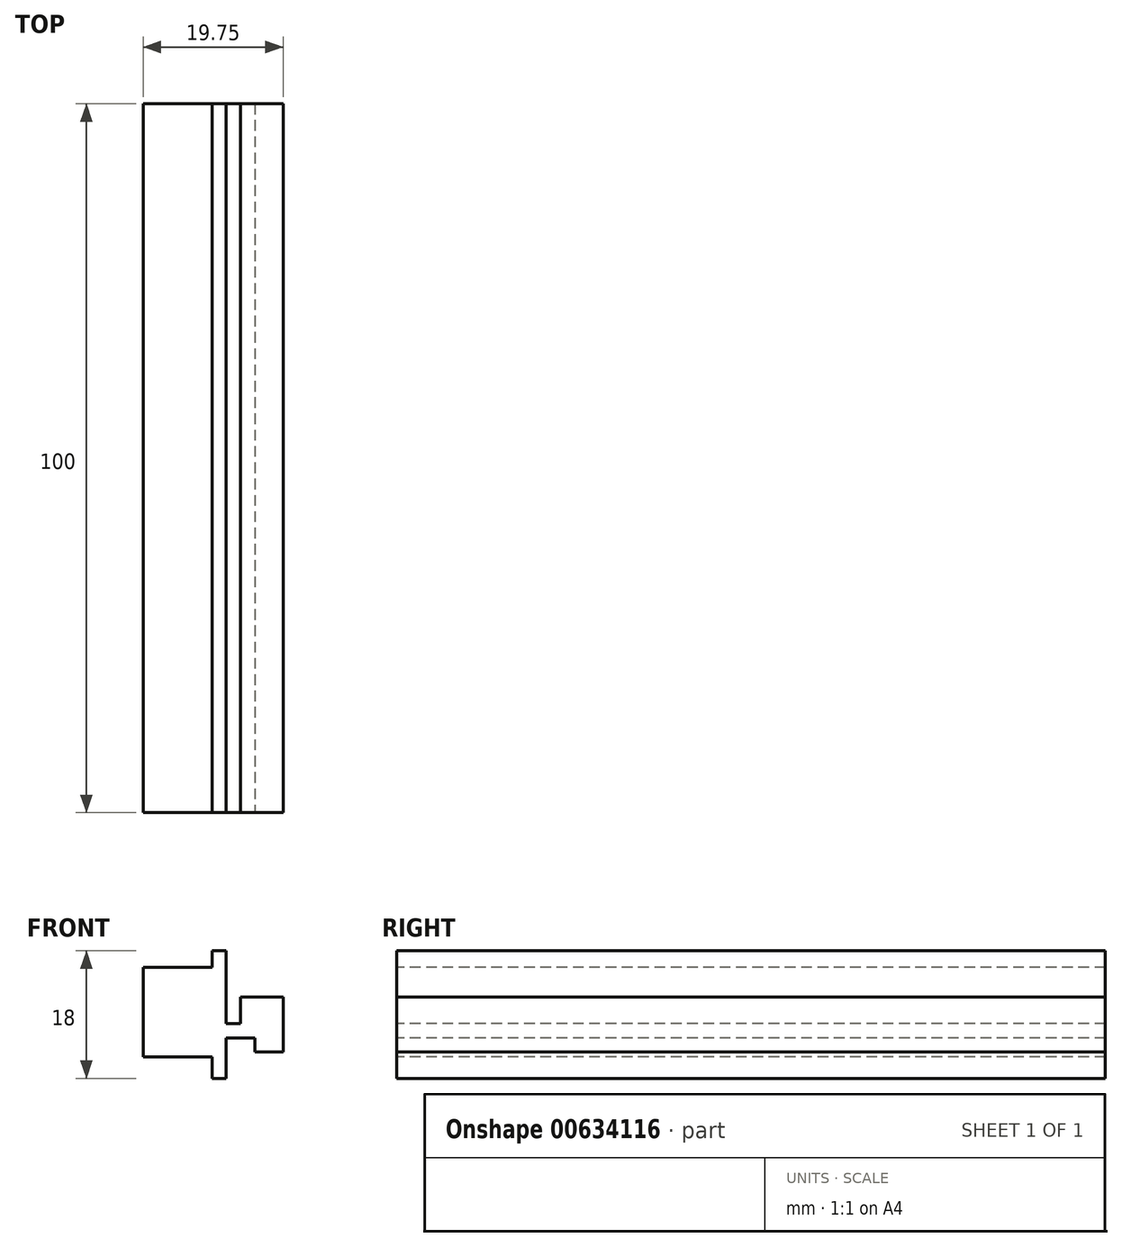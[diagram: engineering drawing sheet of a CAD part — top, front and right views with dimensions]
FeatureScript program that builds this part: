
annotation { "Feature Type Name" : "Feature", "Feature Type Description" : "" }
export const myFeature = defineFeature(function(context is Context, id is Id, definition is map)
    precondition{}
    {
        {
            var Q0;
            Q0=qCreatedBy(makeId("Front.planeOp"),FACE);
            var sketch = newSketch(context, id + "F0", { "sketchPlane" : qUnion([Q0])});
            skLineSegment(sketch, "E0.bottom", {"start": v(-15, 40) * mm, "end": v(15, 40) * mm});
            skLineSegment(sketch, "E0.top", {"start": v(-12, 0) * mm, "end": v(12, 0) * mm});
            skLineSegment(sketch, "E0.left", {"start": v(-15, 40) * mm, "end": v(-15, 37) * mm});
            skLineSegment(sketch, "E0.right", {"start": v(15, 37) * mm, "end": v(15, 3) * mm});
            skLineSegment(sketch, "E1.0", {"start": v(-15, 37) * mm, "end": v(3, 37) * mm});
            skLineSegment(sketch, "E1.1", {"start": v(-12, 6) * mm, "end": v(-12, 6) * mm});
            skLineSegment(sketch, "E1.2", {"start": v(-9, 3) * mm, "end": v(9, 3) * mm});
            skLineSegment(sketch, "E1.3", {"start": v(12, 29.6) * mm, "end": v(12, 6) * mm});
            skLineSegment(sketch, "E2.0", {"start": v(-15, 6) * mm, "end": v(-12, 6) * mm});
            skLineSegment(sketch, "E3", {"start": v(12, 40) * mm, "end": v(7.5, 40) * mm, "construction": true});
            skLineSegment(sketch, "E4", {"start": v(7, 34.8) * mm, "end": v(7, 40) * mm, "construction": true});
            skArc(sketch, "E5", {"start": v(7, 40) * mm, "mid": v(6.75, 29.6) * mm, "end": v(7.5, 39.98) * mm});
            skLineSegment(sketch, "E6.trimOffspring", {"start": v(-15, 6) * mm, "end": v(-15, 3) * mm});
            skPoint(sketch, "E7.orphan", {"position": v(5, 29.7) * mm});
            skPoint(sketch, "E8.visualSharp", {"position": v(15, 40) * mm});
            skArc(sketch, "E8.filletArc", {"start": v(15, 37) * mm, "mid": v(14.12, 39.12) * mm, "end": v(12, 40) * mm});
            skPoint(sketch, "E9.visualSharp", {"position": v(15, 0) * mm});
            skArc(sketch, "E9.filletArc", {"start": v(12, 0) * mm, "mid": v(14.12, 0.88) * mm, "end": v(15, 3) * mm});
            skArc(sketch, "E10.filletArc", {"start": v(9, 3) * mm, "mid": v(11.12, 3.88) * mm, "end": v(12, 6) * mm});
            skPoint(sketch, "E11.visualSharp", {"position": v(-12, 3) * mm});
            skArc(sketch, "E11.filletArc", {"start": v(-12, 6) * mm, "mid": v(-11.12, 3.88) * mm, "end": v(-9, 3) * mm});
            skPoint(sketch, "E12.visualSharp", {"position": v(-15, 0) * mm});
            skArc(sketch, "E12.filletArc", {"start": v(-15, 3) * mm, "mid": v(-14.12, 0.88) * mm, "end": v(-12, 0) * mm});
            skLineSegment(sketch, "E13.0", {"start": v(6.5, 34.8) * mm, "end": v(6.5, 39.8) * mm});
            skLineSegment(sketch, "E14.0", {"start": v(7.5, 34.8) * mm, "end": v(7.5, 40) * mm});
            skLineSegment(sketch, "E15", {"start": v(-15, 6) * mm, "end": v(-15, 16) * mm});
            skLineSegment(sketch, "E16", {"start": v(-15, 16) * mm, "end": v(-12, 16) * mm});
            skLineSegment(sketch, "E17", {"start": v(-12, 16) * mm, "end": v(-12, 6) * mm});
            skLineSegment(sketch, "E18", {"start": v(6.75, 29.6) * mm, "end": v(12, 29.6) * mm});
            skSolve(sketch);
        }
        {
            var Q0;
            Q0=qCreatedBy(makeId("Front.planeOp"),FACE);
            var sketch = newSketch(context, id + "F1", { "sketchPlane" : qUnion([Q0])});
            skLineSegment(sketch, "E19.1.1", {"start": v(7.5, 40) * mm, "end": v(-15, 40) * mm});
            skLineSegment(sketch, "E19.1.2", {"start": v(-15, 40) * mm, "end": v(-15, 37) * mm});
            skArc(sketch, "E19.2.8", {"start": v(-15, 3) * mm, "mid": v(-14.12, 0.88) * mm, "end": v(-12, 0) * mm, "construction": true});
            skLineSegment(sketch, "E19.2.9", {"start": v(-12, 0) * mm, "end": v(-5, 0) * mm});
            skLineSegment(sketch, "E19.2.13", {"start": v(17, 40) * mm, "end": v(8.5, 40) * mm});
            skLineSegment(sketch, "E19.3.0", {"start": v(-15, 18) * mm, "end": v(-15, 7.7) * mm});
            skPoint(sketch, "E20.2", {"position": v(6.5, 37.3) * mm});
            skPoint(sketch, "E21.orphan", {"position": v(6.5, 39.8) * mm});
            skPoint(sketch, "E19.0.2.end.orphan", {"position": v(7, 40) * mm});
            skPoint(sketch, "E22.orphan", {"position": v(12, 29.6) * mm});
            skPoint(sketch, "E23.orphan", {"position": v(7.5, 34.8) * mm});
            skPoint(sketch, "E20.0.start.orphan", {"position": v(6.5, 34.8) * mm});
            skLineSegment(sketch, "E24", {"start": v(-15, 37) * mm, "end": v(-15, 31) * mm});
            skLineSegment(sketch, "E25", {"start": v(0, 0) * mm, "end": v(0, 15) * mm, "construction": true});
            skLineSegment(sketch, "E26", {"start": v(7.5, 40) * mm, "end": v(7.5, 37.97) * mm});
            skLineSegment(sketch, "E27", {"start": v(8.5, 40) * mm, "end": v(8.5, 37.97) * mm});
            skLineSegment(sketch, "E28", {"start": v(15, 32.5) * mm, "end": v(8, 32.5) * mm, "construction": true});
            skPoint(sketch, "E29.orphan", {"position": v(7.6, 39) * mm});
            skLineSegment(sketch, "E30", {"start": v(8, 39) * mm, "end": v(8, 32.5) * mm, "construction": true});
            skPoint(sketch, "E19.3.3.end.orphan", {"position": v(-15, 16) * mm});
            skPoint(sketch, "E19.3.3.start.orphan", {"position": v(-12, 16) * mm});
            skLineSegment(sketch, "E31", {"start": v(-15, 3) * mm, "end": v(-15, 0) * mm});
            skLineSegment(sketch, "E32", {"start": v(-12, 0) * mm, "end": v(-15, 0) * mm});
            skLineSegment(sketch, "E33", {"start": v(-15, 40) * mm, "end": v(-15, 31) * mm, "construction": true});
            skLineSegment(sketch, "E34", {"start": v(-15, 40) * mm, "end": v(-15, 31) * mm});
            skLineSegment(sketch, "E35.trimOffspring", {"start": v(-15, 31) * mm, "end": v(-15, 26) * mm});
            skLineSegment(sketch, "E36.trimOffspring", {"start": v(-15, 29) * mm, "end": v(-15, 24) * mm});
            skPoint(sketch, "E37.orphan", {"position": v(12, 40) * mm});
            skPoint(sketch, "E38.orphan", {"position": v(12, 0) * mm});
            skLineSegment(sketch, "E39.0", {"start": v(13.1, 38) * mm, "end": v(13.1, 38) * mm});
            skLineSegment(sketch, "E40.1", {"start": v(-13, 2) * mm, "end": v(-11, 2) * mm, "construction": true});
            skLineSegment(sketch, "E41.0", {"start": v(-13, 38) * mm, "end": v(-13, 34) * mm});
            skArc(sketch, "E42", {"start": v(13.32, 33.87) * mm, "mid": v(11.56, 36.69) * mm, "end": v(8.5, 37.97) * mm});
            skLineSegment(sketch, "E43.0", {"start": v(29.42, 20) * mm, "end": v(-7, 20) * mm, "construction": true});
            skLineSegment(sketch, "E44.trimOffspring", {"start": v(-13, 0.17) * mm, "end": v(-13, 0) * mm});
            skArc(sketch, "E45.0", {"start": v(2.9, 38) * mm, "mid": v(3.81, 26.3) * mm, "end": v(15, 29.84) * mm});
            skLineSegment(sketch, "E46.trimOffspring", {"start": v(2.9, 38) * mm, "end": v(-13, 38) * mm});
            skLineSegment(sketch, "E47.trimOffspring", {"start": v(13.32, 33.87) * mm, "end": v(13.43, 31.7) * mm});
            skArc(sketch, "E48.trimOffspring", {"start": v(13.1, 38) * mm, "mid": v(13.1, 38) * mm, "end": v(13.1, 38) * mm});
            skArc(sketch, "E49.trimOffspring", {"start": v(7.5, 37.97) * mm, "mid": v(4.01, 28.73) * mm, "end": v(13.43, 31.7) * mm});
            skPoint(sketch, "E50.orphan", {"position": v(7.5, 39) * mm});
            skPoint(sketch, "E51.start.orphan", {"position": v(8.5, 39) * mm});
            skLineSegment(sketch, "E52.0", {"start": v(8, 0) * mm, "end": v(8, 13.5) * mm});
            skLineSegment(sketch, "E53.0", {"start": v(-5, 0) * mm, "end": v(-5, 13.5) * mm});
            skLineSegment(sketch, "E54.0", {"start": v(16.47, 12) * mm, "end": v(14.46, 12) * mm, "construction": true});
            skLineSegment(sketch, "E55.trimOffspring", {"start": v(12.84, 12) * mm, "end": v(10, 12) * mm});
            skLineSegment(sketch, "E56.0", {"start": v(1.5, 0) * mm, "end": v(1.5, 20) * mm, "construction": true});
            skLineSegment(sketch, "E57", {"start": v(1.5, 20) * mm, "end": v(-9.16, 15.5) * mm});
            skLineSegment(sketch, "E58", {"start": v(1.5, 20) * mm, "end": v(10.84, 15.5) * mm});
            skLineSegment(sketch, "E59.0", {"start": v(-9.16, 13.5) * mm, "end": v(-5, 13.5) * mm});
            skLineSegment(sketch, "E60", {"start": v(-9.16, 15.5) * mm, "end": v(-9.16, 13.5) * mm});
            skLineSegment(sketch, "E61", {"start": v(10.84, 15.5) * mm, "end": v(10.84, 13.5) * mm});
            skLineSegment(sketch, "E62.trimOffspring", {"start": v(8, 13.5) * mm, "end": v(10.84, 13.5) * mm});
            skLineSegment(sketch, "E63.trimOffspring", {"start": v(10, 2) * mm, "end": v(15, 2) * mm});
            skLineSegment(sketch, "E64.trimOffspring", {"start": v(8, 0) * mm, "end": v(17, 0) * mm});
            skLineSegment(sketch, "E65.0", {"start": v(10, 2) * mm, "end": v(10, 12) * mm});
            skLineSegment(sketch, "E66.0", {"start": v(1.55, 22.2) * mm, "end": v(-7, 18.58) * mm});
            skLineSegment(sketch, "E66.1", {"start": v(1.55, 22.2) * mm, "end": v(12.84, 16.75) * mm});
            skLineSegment(sketch, "E67.0", {"start": v(-11.16, 16.82) * mm, "end": v(-11.16, 15.5) * mm});
            skLineSegment(sketch, "E68.0", {"start": v(-13, 11.5) * mm, "end": v(-7, 11.5) * mm});
            skLineSegment(sketch, "E69", {"start": v(-11.16, 15.5) * mm, "end": v(-11.16, 13.5) * mm});
            skLineSegment(sketch, "E70.0", {"start": v(12.84, 16.75) * mm, "end": v(12.84, 12) * mm});
            skLineSegment(sketch, "E71.0", {"start": v(-13, 6.7) * mm, "end": v(-7, 6.7) * mm, "construction": true});
            skLineSegment(sketch, "E72.0", {"start": v(-15, 7.7) * mm, "end": v(-13, 7.7) * mm});
            skLineSegment(sketch, "E73.0", {"start": v(-15, 5.7) * mm, "end": v(-11, 5.7) * mm});
            skLineSegment(sketch, "E74.0", {"start": v(-15, 3.7) * mm, "end": v(-13, 3.7) * mm, "construction": true});
            skLineSegment(sketch, "E75.trimOffspring", {"start": v(-15, 5.7) * mm, "end": v(-15, 3) * mm});
            skLineSegment(sketch, "E76.trimOffspring", {"start": v(-13, 3.7) * mm, "end": v(-13, 2) * mm, "construction": true});
            skLineSegment(sketch, "E77.trimOffspring", {"start": v(-11, 5.7) * mm, "end": v(-11, 2) * mm});
            skLineSegment(sketch, "E78.0", {"start": v(-13, 13.5) * mm, "end": v(-11.16, 13.5) * mm});
            skLineSegment(sketch, "E79.trimOffspring", {"start": v(-9.16, 13.5) * mm, "end": v(-7, 13.5) * mm});
            skLineSegment(sketch, "E80.trimOffspring", {"start": v(-13, 11.5) * mm, "end": v(-13, 7.7) * mm});
            skLineSegment(sketch, "E81.0", {"start": v(-7, 11.5) * mm, "end": v(-7, 3.7) * mm});
            skLineSegment(sketch, "E82.trimOffspring", {"start": v(-11, 3.7) * mm, "end": v(-7, 3.7) * mm});
            skLineSegment(sketch, "E83.0", {"start": v(17, 40) * mm, "end": v(17, 0) * mm});
            skPoint(sketch, "E84.orphan", {"position": v(17.1, 0) * mm});
            skLineSegment(sketch, "E85.trimOffspring", {"start": v(15, 29.84) * mm, "end": v(15, 2) * mm});
            skPoint(sketch, "E86.start.orphan", {"position": v(15, 40) * mm});
            skLineSegment(sketch, "E87", {"start": v(-13, 13.5) * mm, "end": v(-13, 18) * mm});
            skLineSegment(sketch, "E88.trimOffspring", {"start": v(-15, 22) * mm, "end": v(-15, 21.16) * mm, "construction": true});
            skLineSegment(sketch, "E89.trimOffspring", {"start": v(-15, 22) * mm, "end": v(-15, 18) * mm});
            skPoint(sketch, "E90.start.orphan", {"position": v(-12, 28) * mm});
            skPoint(sketch, "E91.orphan", {"position": v(-12, 29) * mm});
            skLineSegment(sketch, "E92.0", {"start": v(-9, 26) * mm, "end": v(-11, 26) * mm});
            skLineSegment(sketch, "E93.0", {"start": v(-11, 24) * mm, "end": v(-13, 24) * mm});
            skLineSegment(sketch, "E94", {"start": v(-9, 20) * mm, "end": v(-9, 26) * mm});
            skLineSegment(sketch, "E95.0", {"start": v(-11, 20) * mm, "end": v(-11, 22) * mm});
            skLineSegment(sketch, "E96.trimOffspring", {"start": v(-11, 24) * mm, "end": v(-11, 26) * mm});
            skLineSegment(sketch, "E97.trimOffspring", {"start": v(-13, 28) * mm, "end": v(-13, 34) * mm});
            skLineSegment(sketch, "E98", {"start": v(-15, 22) * mm, "end": v(-11, 22) * mm});
            skLineSegment(sketch, "E99", {"start": v(-13, 24) * mm, "end": v(-15, 24) * mm});
            skLineSegment(sketch, "E100.0", {"start": v(-7, 18.58) * mm, "end": v(-7, 28) * mm});
            skLineSegment(sketch, "E101.0", {"start": v(-13, 18) * mm, "end": v(-8.36, 18) * mm});
            skLineSegment(sketch, "E102.trimOffspring", {"start": v(-8.36, 18) * mm, "end": v(-11.16, 16.82) * mm});
            skLineSegment(sketch, "E103.0", {"start": v(-11, 20) * mm, "end": v(-9, 20) * mm});
            skLineSegment(sketch, "E104.0", {"start": v(-7, 28) * mm, "end": v(-13, 28) * mm});
            skSolve(sketch);
        }
        {
            var Q0;
            Q0=qSketchRegion(id+"F1",true);
            extrude(context, id + "F2", {"entities" : qUnion([Q0]), "oppositeDirection" : true, "depth" : 1910 * mm, "offsetDistance" : 25 * mm});
        }
        {
            var Q0;
            Q0=makeQuery(id+"F1.imprint","IMPRINT",FACE,{"disambiguationData":[TD([[makeQuery(id+"F1.imprint","IMPRINT",EDGE,{"derivedFrom":sQuery(id+"F1.wireOp",EDGE,"E19.1.1")}),1.0]])]});
            var sketch = newSketch(context, id + "F3", { "sketchPlane" : qUnion([Q0])});
            skLineSegment(sketch, "E105.0", {"start": v(-13.5, 18) * mm, "end": v(-13.5, -0.51) * mm});
            skSolve(sketch);
        }
        {
            var Q0;
            Q0=makeQuery(id+"F3.imprint","IMPRINT",FACE,{"disambiguationData":[TD([[makeQuery(id+"F3.imprint","IMPRINT",EDGE,{"derivedFrom":makeQuery(id+"F1.imprint","IMPRINT",EDGE,{"derivedFrom":sQuery(id+"F1.wireOp",EDGE,"E19.1.1")})}),1.0]])]});
            var sketch = newSketch(context, id + "F4", { "sketchPlane" : qUnion([Q0])});
            skLineSegment(sketch, "E106.0", {"start": v(-17, 40) * mm, "end": v(-25.5, 40) * mm});
            skLineSegment(sketch, "E107.0", {"start": v(-49.1, 40) * mm, "end": v(-49.1, 18) * mm});
            skLineSegment(sketch, "E108.0", {"start": v(-17, 40) * mm, "end": v(-17, 18) * mm});
            skPoint(sketch, "E109.orphan", {"position": v(7.5, 40) * mm});
            skLineSegment(sketch, "E110.1", {"start": v(-19, 29.83) * mm, "end": v(-19, 20) * mm});
            skLineSegment(sketch, "E110.3", {"start": v(-47.1, 38) * mm, "end": v(-47.1, 20) * mm});
            skArc(sketch, "E111.0", {"start": v(7.5, 37.97) * mm, "mid": v(4.01, 28.73) * mm, "end": v(13.43, 31.7) * mm, "construction": true});
            skLineSegment(sketch, "E112.0", {"start": v(17, 40) * mm, "end": v(8.5, 40) * mm});
            skLineSegment(sketch, "E113.0", {"start": v(7.5, 40) * mm, "end": v(-15, 40) * mm});
            skLineSegment(sketch, "E114.0", {"start": v(-26.6, 40) * mm, "end": v(-26.6, 37.97) * mm});
            skLineSegment(sketch, "E115.0", {"start": v(-25.5, 40) * mm, "end": v(-25.5, 37.98) * mm});
            skLineSegment(sketch, "E116.0", {"start": v(-7, 18.58) * mm, "end": v(-7, 28) * mm});
            skLineSegment(sketch, "E117", {"start": v(-47.1, 23.29) * mm, "end": v(15, 23.29) * mm, "construction": true});
            skPoint(sketch, "E118.orphan", {"position": v(-7, 23.29) * mm});
            skLineSegment(sketch, "E119", {"start": v(8, 32.5) * mm, "end": v(2.5, 32.5) * mm});
            skLineSegment(sketch, "E120.0", {"start": v(8, 39) * mm, "end": v(8, 32.5) * mm});
            skLineSegment(sketch, "E120.1", {"start": v(17, 40) * mm, "end": v(17, 0) * mm});
            skLineSegment(sketch, "E121.trimOffspring", {"start": v(-17, 32.5) * mm, "end": v(-26, 32.5) * mm, "construction": true});
            skArc(sketch, "E122", {"start": v(-26.6, 37.97) * mm, "mid": v(-25.95, 27.01) * mm, "end": v(-25.5, 37.98) * mm});
            skArc(sketch, "E123.0", {"start": v(-31.1, 38) * mm, "mid": v(-30.2, 26.3) * mm, "end": v(-19, 29.83) * mm});
            skLineSegment(sketch, "E124.trimOffspring", {"start": v(-26.6, 40) * mm, "end": v(-49.1, 40) * mm});
            skLineSegment(sketch, "E125.trimOffspring", {"start": v(-26.6, 27.05) * mm, "end": v(-26.6, 20) * mm, "construction": true});
            skLineSegment(sketch, "E126.trimOffspring", {"start": v(-25.5, 27.04) * mm, "end": v(-25.5, 20) * mm, "construction": true});
            skLineSegment(sketch, "E127.trimOffspring", {"start": v(-31.1, 38) * mm, "end": v(-47.1, 38) * mm});
            skLineSegment(sketch, "E128.0", {"start": v(-49.1, 18) * mm, "end": v(-17, 18) * mm});
            skPoint(sketch, "E129.orphan", {"position": v(-8.36, 18) * mm});
            skPoint(sketch, "E130.orphan", {"position": v(-13, 18) * mm});
            skLineSegment(sketch, "E131.0", {"start": v(-47.1, 20) * mm, "end": v(-19, 20) * mm});
            skSolve(sketch);
        }
        {
            var Q0;
            Q0=makeQuery(id+"F1.imprint","IMPRINT",FACE,{"disambiguationData":[TD([[makeQuery(id+"F1.imprint","IMPRINT",EDGE,{"derivedFrom":sQuery(id+"F1.wireOp",EDGE,"E19.1.1")}),1.0]])]});
            var sketch = newSketch(context, id + "F5", { "sketchPlane" : qUnion([Q0])});
            skArc(sketch, "E132.0", {"start": v(7.5, 37.97) * mm, "mid": v(4.01, 28.73) * mm, "end": v(13.43, 31.7) * mm, "construction": true});
            skArc(sketch, "E132.1", {"start": v(13.32, 33.87) * mm, "mid": v(11.56, 36.69) * mm, "end": v(8.5, 37.97) * mm, "construction": true});
            skLineSegment(sketch, "E132.2", {"start": v(7.5, 40) * mm, "end": v(-15, 40) * mm});
            skArc(sketch, "E132.3", {"start": v(-26.6, 37.97) * mm, "mid": v(-25.95, 27.01) * mm, "end": v(-25.5, 37.98) * mm, "construction": true});
            skLineSegment(sketch, "E133.0", {"start": v(-15, 40) * mm, "end": v(-25.5, 40) * mm});
            skPoint(sketch, "E134.orphan", {"position": v(-26.6, 40) * mm});
            skLineSegment(sketch, "E135.0", {"start": v(7.5, 40) * mm, "end": v(7.5, 37.37) * mm});
            skLineSegment(sketch, "E135.1", {"start": v(8.5, 40) * mm, "end": v(8.5, 37.37) * mm});
            skLineSegment(sketch, "E135.2", {"start": v(-25.5, 40) * mm, "end": v(-25.5, 37.37) * mm});
            skLineSegment(sketch, "E135.3", {"start": v(-26.6, 40) * mm, "end": v(-26.6, 37.36) * mm});
            skPoint(sketch, "E135.4", {"position": v(-25.5, 38.99) * mm});
            skLineSegment(sketch, "E136", {"start": v(-49.1, 40) * mm, "end": v(-216.5, 40) * mm});
            skLineSegment(sketch, "E137.0", {"start": v(8.5, 41) * mm, "end": v(-216.5, 41) * mm});
            skLineSegment(sketch, "E138", {"start": v(8.5, 40) * mm, "end": v(8.5, 41) * mm});
            skLineSegment(sketch, "E139", {"start": v(-216.5, 41) * mm, "end": v(-216.5, 40) * mm, "construction": true});
            skArc(sketch, "E140.0", {"start": v(7.5, 37.37) * mm, "mid": v(4.47, 29.12) * mm, "end": v(12.84, 31.8) * mm});
            skArc(sketch, "E141.0", {"start": v(12.74, 33.72) * mm, "mid": v(11.2, 36.21) * mm, "end": v(8.5, 37.37) * mm});
            skArc(sketch, "E142", {"start": v(12.74, 33.72) * mm, "mid": v(12.88, 32.76) * mm, "end": v(12.84, 31.8) * mm});
            skPoint(sketch, "E143.orphan", {"position": v(7.5, 37.97) * mm});
            skPoint(sketch, "E144.orphan", {"position": v(8.5, 37.97) * mm});
            skArc(sketch, "E145.0", {"start": v(-26.6, 37.36) * mm, "mid": v(-25.95, 27.61) * mm, "end": v(-25.5, 37.37) * mm});
            skPoint(sketch, "E146.orphan", {"position": v(-26.6, 37.97) * mm});
            skPoint(sketch, "E147.orphan", {"position": v(-25.5, 37.98) * mm});
            skLineSegment(sketch, "E148.trimOffspring", {"start": v(-26.6, 40) * mm, "end": v(-49.1, 40) * mm});
            skSolve(sketch);
        }
        {
            var Q0;
            {var subQ7=sQuery(id+"F5.wireOp",EDGE,"E132.2");Q0=makeQuery(id+"F5.imprint","IMPRINT",FACE,{"disambiguationData":[TD([[makeQuery(id+"F5.imprint","IMPRINT",EDGE,{"derivedFrom":subQ7}),1.0]])]});}
            var sketch = newSketch(context, id + "F6", { "sketchPlane" : qUnion([Q0])});
            skLineSegment(sketch, "E149.0", {"start": v(-13, 11.5) * mm, "end": v(-7, 11.5) * mm});
            skLineSegment(sketch, "E149.1", {"start": v(-7, 11.5) * mm, "end": v(-7, 3.7) * mm});
            skLineSegment(sketch, "E149.2", {"start": v(-11, 3.7) * mm, "end": v(-7, 3.7) * mm});
            skLineSegment(sketch, "E149.3", {"start": v(-11, 5.7) * mm, "end": v(-11, 3.7) * mm});
            skLineSegment(sketch, "E149.4", {"start": v(-15, 5.7) * mm, "end": v(-11, 5.7) * mm});
            skLineSegment(sketch, "E149.5", {"start": v(-15, 7.7) * mm, "end": v(-13, 7.7) * mm});
            skLineSegment(sketch, "E149.6", {"start": v(-13, 11.5) * mm, "end": v(-13, 7.7) * mm});
            skPoint(sketch, "E150.orphan", {"position": v(-11, 2) * mm});
            skLineSegment(sketch, "E151.0", {"start": v(-15, 18) * mm, "end": v(-15, 7.7) * mm});
            skLineSegment(sketch, "E151.1", {"start": v(-15, 3) * mm, "end": v(-15, 0) * mm});
            skLineSegment(sketch, "E151.2", {"start": v(-15, 5.7) * mm, "end": v(-15, 3) * mm});
            skLineSegment(sketch, "E152.0", {"start": v(-17, 18) * mm, "end": v(-17, 15.63) * mm});
            skLineSegment(sketch, "E153.0", {"start": v(-17, 3) * mm, "end": v(-17, 0) * mm});
            skLineSegment(sketch, "E154", {"start": v(-17, 18) * mm, "end": v(-15, 18) * mm});
            skLineSegment(sketch, "E155", {"start": v(-17, 0) * mm, "end": v(-15, 0) * mm});
            skLineSegment(sketch, "E156", {"start": v(-17, 3) * mm, "end": v(-26.75, 3) * mm});
            skLineSegment(sketch, "E157", {"start": v(-26.75, 3) * mm, "end": v(-26.75, 15.63) * mm});
            skLineSegment(sketch, "E158", {"start": v(-26.75, 15.63) * mm, "end": v(-17, 15.63) * mm});
            skSolve(sketch);
        }
        {
            var Q0;
            Q0 = qSketchRegion(id + "F6", true);
            extrude(context, id + "F7", {"entities" : qUnion([Q0]), "operationType" : NewBodyOperationType.ADD, "oppositeDirection" : true, "depth" : 100 * mm, "offsetDistance" : 25 * mm});
        }
        {
            var Q0;
            {var subQ7=sQuery(id+"F5.wireOp",EDGE,"E132.2");Q0=makeQuery(id+"F5.imprint","IMPRINT",FACE,{"disambiguationData":[TD([[makeQuery(id+"F5.imprint","IMPRINT",EDGE,{"derivedFrom":subQ7}),1.0]])]});}
            extrude(context, id + "F8", {"entities" : qUnion([Q0]), "operationType" : NewBodyOperationType.REMOVE, "oppositeDirection" : true, "depth" : 2255 * mm, "offsetDistance" : 25 * mm});
        }
    });
